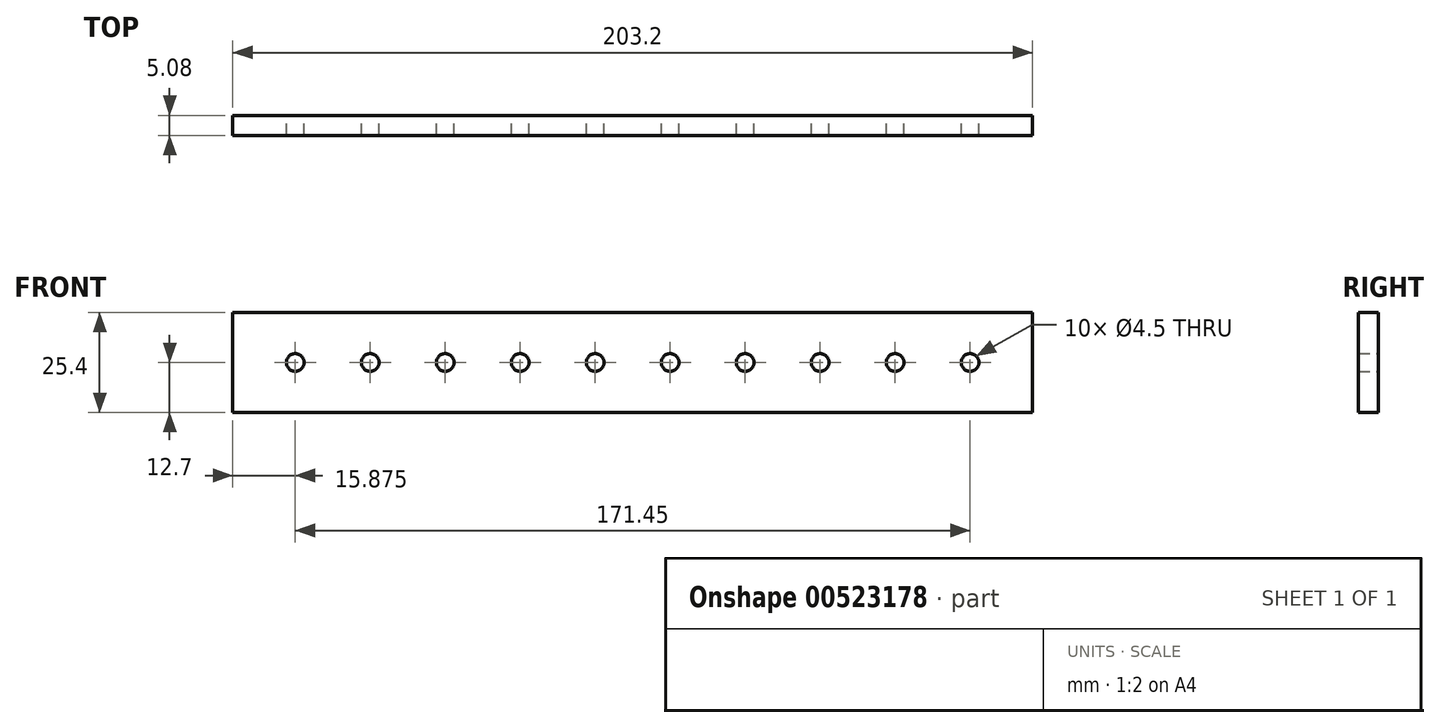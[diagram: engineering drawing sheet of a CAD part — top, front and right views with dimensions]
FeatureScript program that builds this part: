
annotation { "Feature Type Name" : "Feature", "Feature Type Description" : "" }
export const myFeature = defineFeature(function(context is Context, id is Id, definition is map)
    precondition{}
    {
        {
            var Q0;
            Q0=qCreatedBy(makeId("Front.planeOp"),FACE);
            var sketch = newSketch(context, id + "F0", { "sketchPlane" : qUnion([Q0])});
            skLineSegment(sketch, "E0", {"start": v(0, 0) * mm, "end": v(0, 25.4) * mm});
            skLineSegment(sketch, "E1", {"start": v(0, 25.4) * mm, "end": v(203.2, 25.4) * mm});
            skLineSegment(sketch, "E2", {"start": v(203.2, 25.4) * mm, "end": v(203.2, 0) * mm});
            skLineSegment(sketch, "E3", {"start": v(203.2, 0) * mm, "end": v(0, 0) * mm});
            skLineSegment(sketch, "E4", {"start": v(0, 25.4) * mm, "end": v(15.88, 25.4) * mm, "construction": true});
            skLineSegment(sketch, "E5", {"start": v(15.88, 25.4) * mm, "end": v(15.88, 12.7) * mm, "construction": true});
            skCircle(sketch, "E6", {"center": v(15.88, 12.7) * mm, "radius": 2.25 * mm});
            skCircle(sketch, "E7.1.0.0", {"center": v(34.92, 12.7) * mm, "radius": 2.25 * mm});
            skCircle(sketch, "E7.2.0.0", {"center": v(53.97, 12.7) * mm, "radius": 2.25 * mm});
            skCircle(sketch, "E7.3.0.0", {"center": v(73.02, 12.7) * mm, "radius": 2.25 * mm});
            skCircle(sketch, "E7.4.0.0", {"center": v(92.07, 12.7) * mm, "radius": 2.25 * mm});
            skCircle(sketch, "E7.5.0.0", {"center": v(111.12, 12.7) * mm, "radius": 2.25 * mm});
            skCircle(sketch, "E7.6.0.0", {"center": v(130.17, 12.7) * mm, "radius": 2.25 * mm});
            skCircle(sketch, "E7.7.0.0", {"center": v(149.22, 12.7) * mm, "radius": 2.25 * mm});
            skCircle(sketch, "E7.8.0.0", {"center": v(168.27, 12.7) * mm, "radius": 2.25 * mm});
            skCircle(sketch, "E7.9.0.0", {"center": v(187.32, 12.7) * mm, "radius": 2.25 * mm});
            skLineSegment(sketch, "E7.direction1", {"start": v(15.88, 12.7) * mm, "end": v(34.92, 12.7) * mm, "construction": true});
            skSolve(sketch);
        }
        {
            var Q0;
            Q0 = qSketchRegion(id + "F0", true);
            extrude(context, id + "F1", {"entities" : qUnion([Q0]), "depth" : 5.08 * mm, "offsetDistance" : 25.4 * mm});
        }
    });
